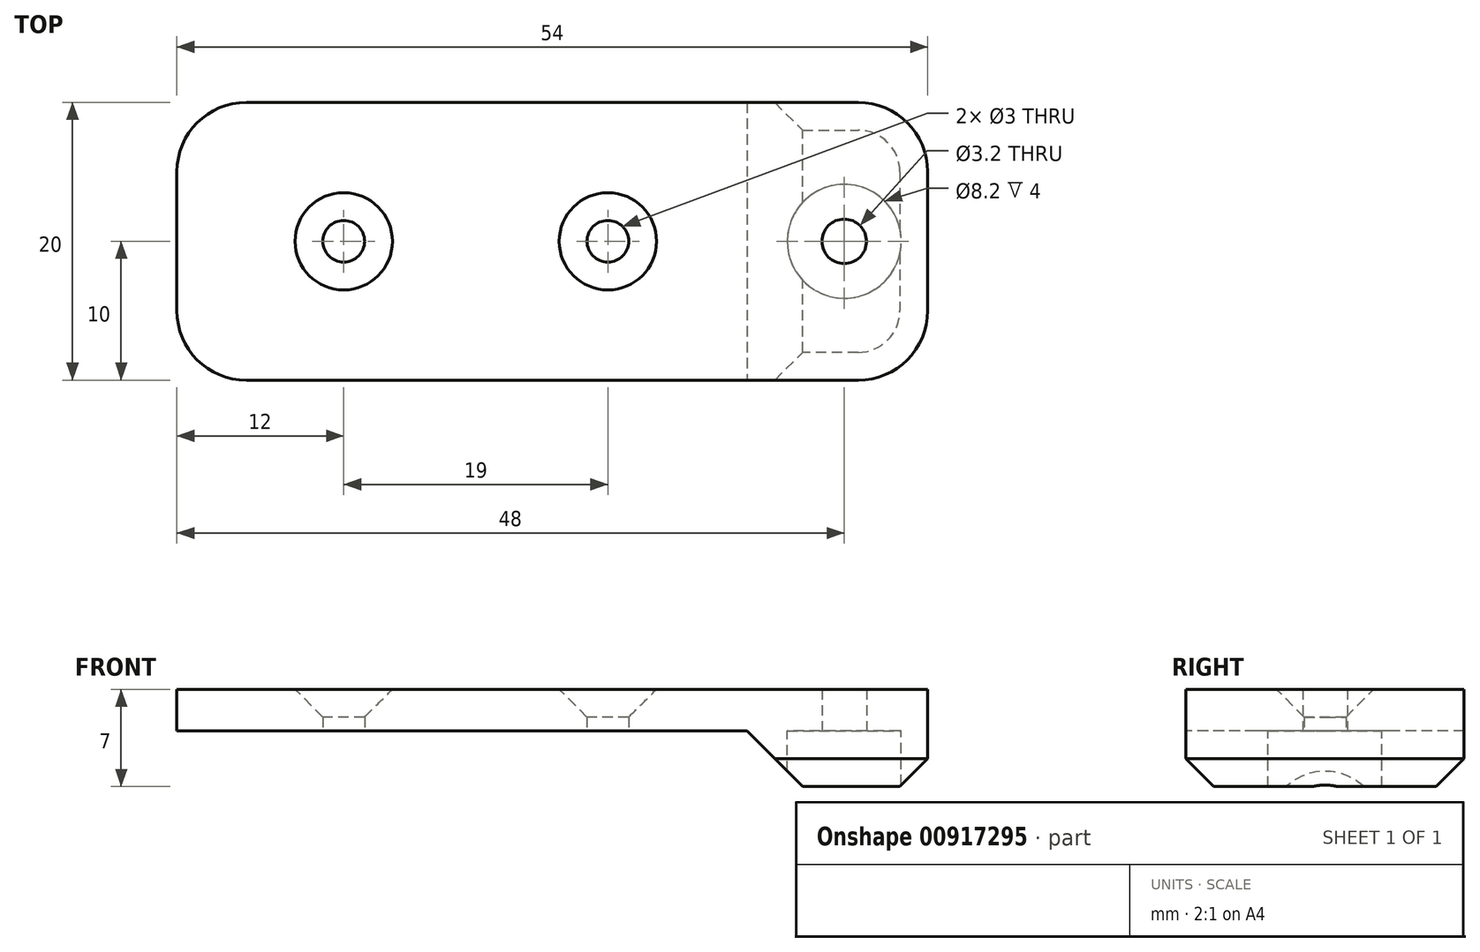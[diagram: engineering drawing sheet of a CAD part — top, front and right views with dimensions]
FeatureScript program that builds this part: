
annotation { "Feature Type Name" : "Feature", "Feature Type Description" : "" }
export const myFeature = defineFeature(function(context is Context, id is Id, definition is map)
    precondition{}
    {
        {
            var Q0;
            Q0=qCreatedBy(makeId("Top.planeOp"),FACE);
            var sketch = newSketch(context, id + "F0", { "sketchPlane" : qUnion([Q0])});
            skLineSegment(sketch, "E0.bottom", {"start": v(-22, 10) * mm, "end": v(22, 10) * mm});
            skLineSegment(sketch, "E0.top", {"start": v(-22, -10) * mm, "end": v(22, -10) * mm});
            skLineSegment(sketch, "E0.left", {"start": v(-27, 5) * mm, "end": v(-27, -5) * mm});
            skLineSegment(sketch, "E0.right", {"start": v(27, 5) * mm, "end": v(27, -5) * mm});
            skPoint(sketch, "E0.middle", {"position": v(0, 0) * mm});
            skPoint(sketch, "E1.visualSharp", {"position": v(-27, 10) * mm});
            skArc(sketch, "E1.filletArc", {"start": v(-22, 10) * mm, "mid": v(-25.54, 8.54) * mm, "end": v(-27, 5) * mm});
            skPoint(sketch, "E2.visualSharp", {"position": v(-27, -10) * mm});
            skArc(sketch, "E2.filletArc", {"start": v(-27, -5) * mm, "mid": v(-25.54, -8.54) * mm, "end": v(-22, -10) * mm});
            skCircle(sketch, "E3", {"center": v(-15, 0) * mm, "radius": 1.5 * mm});
            skCircle(sketch, "E4", {"center": v(4, 0) * mm, "radius": 1.5 * mm});
            skCircle(sketch, "E5", {"center": v(21, 0) * mm, "radius": 1.6 * mm});
            skPoint(sketch, "E6.visualSharp", {"position": v(27, 10) * mm});
            skArc(sketch, "E6.filletArc", {"start": v(27, 5) * mm, "mid": v(25.54, 8.54) * mm, "end": v(22, 10) * mm});
            skPoint(sketch, "E7.visualSharp", {"position": v(27, -10) * mm});
            skArc(sketch, "E7.filletArc", {"start": v(22, -10) * mm, "mid": v(25.54, -8.54) * mm, "end": v(27, -5) * mm});
            skSolve(sketch);
        }
        {
            var Q0;
            Q0=makeQuery(id+"F0.imprint","IMPRINT",FACE,{"disambiguationData":[TD([[makeQuery(id+"F0.imprint","IMPRINT",EDGE,{"derivedFrom":sQuery(id+"F0.wireOp",EDGE,"E0.bottom")}),-1.0]])]});
            extrude(context, id + "F1", {"entities" : qUnion([Q0]), "depth" : 3 * mm, "offsetDistance" : 25 * mm});
        }
        {
            var Q0;
            Q0=makeQuery(id+"F1.opExtrude","CAP_EDGE",EDGE,{"disambiguationData":[OSD([sQuery(id+"F0.wireOp",EDGE,"E3")])],"isStart":false});
            var Q1;
            Q1=makeQuery(id+"F1.opExtrude","CAP_EDGE",EDGE,{"disambiguationData":[OSD([sQuery(id+"F0.wireOp",EDGE,"E4")])],"isStart":false});
            chamfer(context, id + "F2", {"entities" : qUnion([Q0, Q1]), "width" : 2 * mm, "tangentPropagation" : true});
        }
        {
            var Q0;
            Q0=makeQuery(id+"F1.opExtrude","CAP_FACE",FACE,{"disambiguationData":[OSD([sQuery(id+"F0.wireOp",EDGE,"E0.bottom"),sQuery(id+"F0.wireOp",EDGE,"E0.top"),sQuery(id+"F0.wireOp",EDGE,"E0.left"),sQuery(id+"F0.wireOp",EDGE,"E0.right"),sQuery(id+"F0.wireOp",EDGE,"E1.filletArc"),sQuery(id+"F0.wireOp",EDGE,"E2.filletArc"),sQuery(id+"F0.wireOp",EDGE,"E3"),sQuery(id+"F0.wireOp",EDGE,"E4"),sQuery(id+"F0.wireOp",EDGE,"E5"),sQuery(id+"F0.wireOp",EDGE,"E6.filletArc"),sQuery(id+"F0.wireOp",EDGE,"E7.filletArc")])],"isStart":true});
            var sketch = newSketch(context, id + "F3", { "sketchPlane" : qUnion([Q0])});
            skCircle(sketch, "E8.0", {"center": v(21, 0) * mm, "radius": 4.1 * mm});
            skLineSegment(sketch, "E9", {"start": v(14, -10) * mm, "end": v(14, 10) * mm});
            skSolve(sketch);
        }
        {
            var Q0;
            Q0=makeQuery(id+"F3.imprint","IMPRINT",FACE,{"disambiguationData":[TD([[makeQuery(id+"F3.imprint","IMPRINT",EDGE,{"derivedFrom":sQuery(id+"F3.wireOp",EDGE,"E8.0")}),-1.0]])]});
            extrude(context, id + "F4", {"entities" : qUnion([Q0]), "operationType" : NewBodyOperationType.ADD, "depth" : 4 * mm, "offsetDistance" : 25 * mm});
        }
        {
            var Q0;
            Q0=makeQuery(id+"F4.opExtrude","CAP_EDGE",EDGE,{"disambiguationData":[OSD([sQuery(id+"F3.wireOp",EDGE,"E9")])],"isStart":false});
            chamfer(context, id + "F5", {"entities" : qUnion([Q0]), "width" : 4 * mm, "tangentPropagation" : true});
        }
        {
            var Q0;
            Q0=makeQuery(id+"F4.opExtrude","CAP_EDGE",EDGE,{"disambiguationData":[OSD([sQuery(id+"F0.wireOp",EDGE,"E0.top")])],"isStart":false});
            var Q1;
            Q1=makeQuery(id+"F4.opExtrude","CAP_EDGE",EDGE,{"disambiguationData":[OSD([sQuery(id+"F0.wireOp",EDGE,"E7.filletArc")])],"isStart":false});
            var Q2;
            Q2=makeQuery(id+"F4.opExtrude","CAP_EDGE",EDGE,{"disambiguationData":[OSD([sQuery(id+"F0.wireOp",EDGE,"E0.right")])],"isStart":false});
            var Q3;
            Q3=makeQuery(id+"F4.opExtrude","CAP_EDGE",EDGE,{"disambiguationData":[OSD([sQuery(id+"F0.wireOp",EDGE,"E6.filletArc")])],"isStart":false});
            var Q4;
            Q4=makeQuery(id+"F4.opExtrude","CAP_EDGE",EDGE,{"disambiguationData":[OSD([sQuery(id+"F0.wireOp",EDGE,"E0.bottom")])],"isStart":false});
            chamfer(context, id + "F6", {"entities" : qUnion([Q0, Q1, Q2, Q3, Q4]), "width" : 2 * mm, "tangentPropagation" : true});
        }
    });
